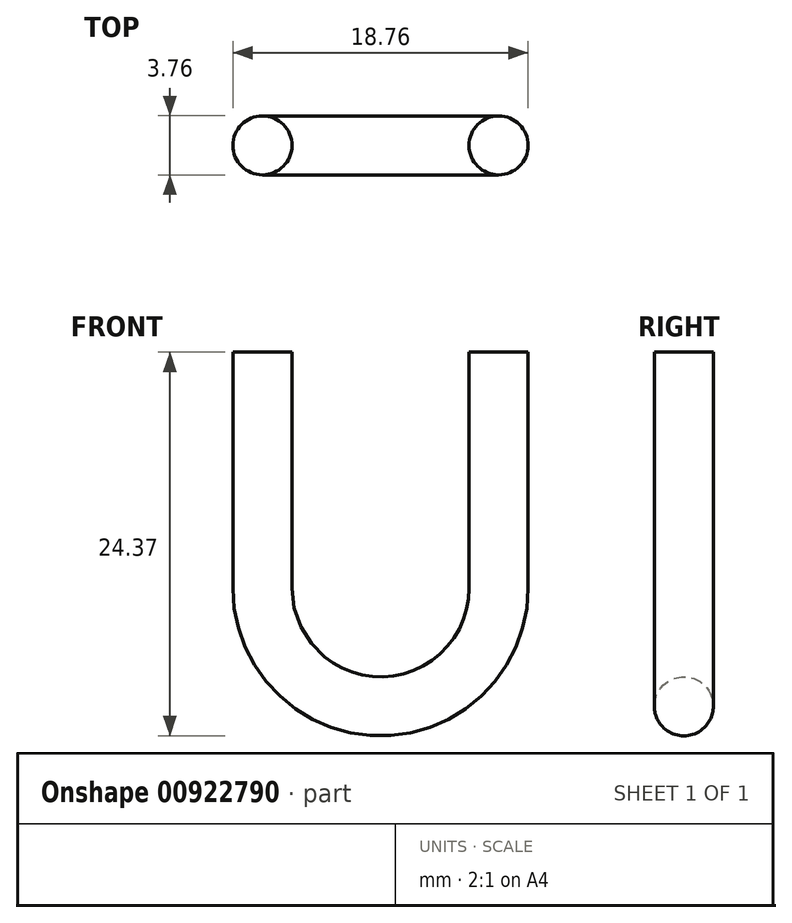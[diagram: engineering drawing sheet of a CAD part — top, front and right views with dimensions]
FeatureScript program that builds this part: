
annotation { "Feature Type Name" : "Feature", "Feature Type Description" : "" }
export const myFeature = defineFeature(function(context is Context, id is Id, definition is map)
    precondition{}
    {
        {
            var Q0;
            Q0=qCreatedBy(makeId("Front.planeOp"),FACE);
            var sketch = newSketch(context, id + "F0", { "sketchPlane" : qUnion([Q0])});
            skLineSegment(sketch, "E0", {"start": v(0, 0) * mm, "end": v(0, -15) * mm});
            skArc(sketch, "E1", {"start": v(0, -15) * mm, "mid": v(-7.5, -22.5) * mm, "end": v(-15, -15) * mm});
            skLineSegment(sketch, "E2", {"start": v(-15, -15) * mm, "end": v(-15, 0) * mm});
            skSolve(sketch);
        }
        {
            var Q0;
            Q0=sQuery(id+"F0.wireOp",VERTEX,"E0.start");
            var Q1;
            Q1=sQuery(id+"F0.wireOp",EDGE,"E0");
            cPlane(context, id + "F1", {"entities" : qUnion([Q0, Q1]), "cplaneType" : CPlaneType.CURVE_POINT, "offset" : 25 * mm, "width" : 150 * mm, "height" : 150 * mm});
        }
        {
            var Q0;
            Q0=qCreatedBy(id+"F1.planeOp",FACE);
            var sketch = newSketch(context, id + "F2", { "sketchPlane" : qUnion([Q0])});
            skCircle(sketch, "E3", {"center": v(-15, 0) * mm, "radius": 1.88 * mm});
            skSolve(sketch);
        }
        {
            var Q0;
            Q0=makeQuery(id+"F2.imprint","IMPRINT",FACE,{"disambiguationData":[TD([[makeQuery(id+"F2.imprint","IMPRINT",EDGE,{"derivedFrom":sQuery(id+"F2.wireOp",EDGE,"E3")}),1.0]])]});
            var Q1;
            Q1=sQuery(id+"F0.wireOp",EDGE,"E2");
            var Q2;
            Q2=sQuery(id+"F0.wireOp",EDGE,"E1");
            var Q3;
            Q3=sQuery(id+"F0.wireOp",EDGE,"E0");
            sweep(context, id + "F3", {"profiles" : qUnion([Q0]), "path" : qUnion([Q1, Q2, Q3])});
        }
    });
